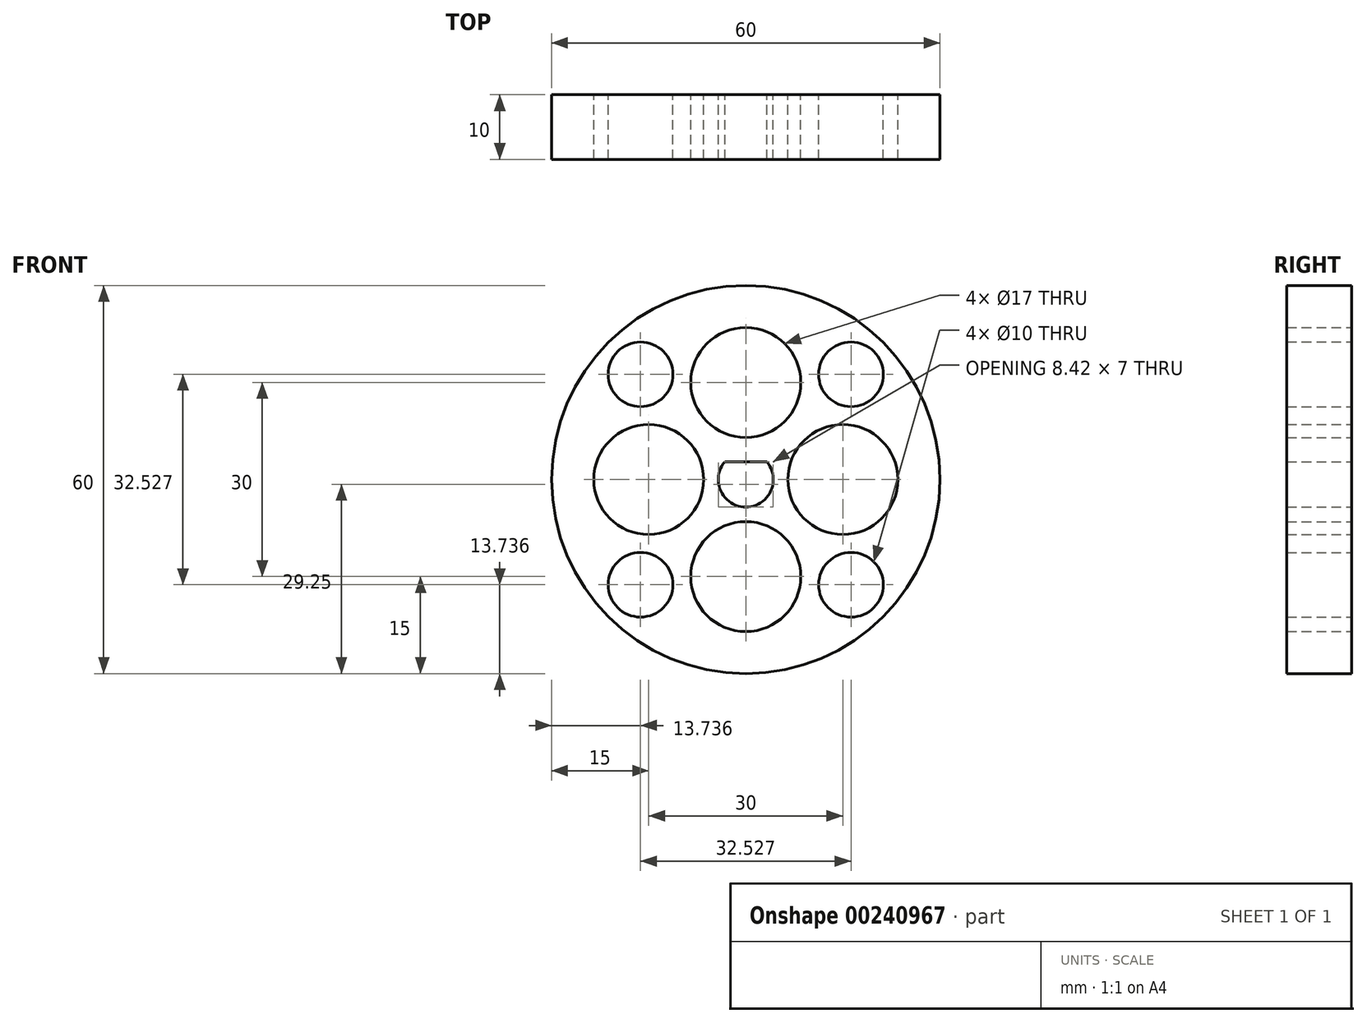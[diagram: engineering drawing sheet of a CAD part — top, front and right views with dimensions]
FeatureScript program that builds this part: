
annotation { "Feature Type Name" : "Feature", "Feature Type Description" : "" }
export const myFeature = defineFeature(function(context is Context, id is Id, definition is map)
    precondition{}
    {
        {
            var Q0;
            Q0=qCreatedBy(makeId("Front.planeOp"),FACE);
            var sketch = newSketch(context, id + "F0", { "sketchPlane" : qUnion([Q0])});
            skCircle(sketch, "E0", {"center": v(0, 0) * mm, "radius": 30 * mm});
            skArc(sketch, "E1", {"start": v(-3.24, 2.75) * mm, "mid": v(0, -4.25) * mm, "end": v(3.24, 2.75) * mm});
            skLineSegment(sketch, "E2", {"start": v(-3.24, 2.75) * mm, "end": v(3.24, 2.75) * mm});
            skCircle(sketch, "E3", {"center": v(0, 15) * mm, "radius": 8.5 * mm});
            skLineSegment(sketch, "E4", {"start": v(0, 0) * mm, "end": v(0, 15) * mm, "construction": true});
            skLineSegment(sketch, "E5", {"start": v(0, 15) * mm, "end": v(0, 30) * mm, "construction": true});
            skCircle(sketch, "E6.1.0", {"center": v(-15, 0) * mm, "radius": 8.5 * mm});
            skCircle(sketch, "E6.2.0", {"center": v(0, -15) * mm, "radius": 8.5 * mm});
            skCircle(sketch, "E6.3.0", {"center": v(15, 0) * mm, "radius": 8.5 * mm});
            skCircle(sketch, "E7", {"center": v(16.26, 16.26) * mm, "radius": 5 * mm});
            skLineSegment(sketch, "E8", {"start": v(0, 0) * mm, "end": v(16.26, 16.26) * mm, "construction": true});
            skCircle(sketch, "E9.1.0", {"center": v(-16.26, 16.26) * mm, "radius": 5 * mm});
            skCircle(sketch, "E9.2.0", {"center": v(-16.26, -16.26) * mm, "radius": 5 * mm});
            skCircle(sketch, "E9.3.0", {"center": v(16.26, -16.26) * mm, "radius": 5 * mm});
            skSolve(sketch);
        }
        {
            var Q0;
            Q0 = qSketchRegion(id + "F0", true);
            extrude(context, id + "F1", {"entities" : qUnion([Q0]), "depth" : 10 * mm});
        }
    });
